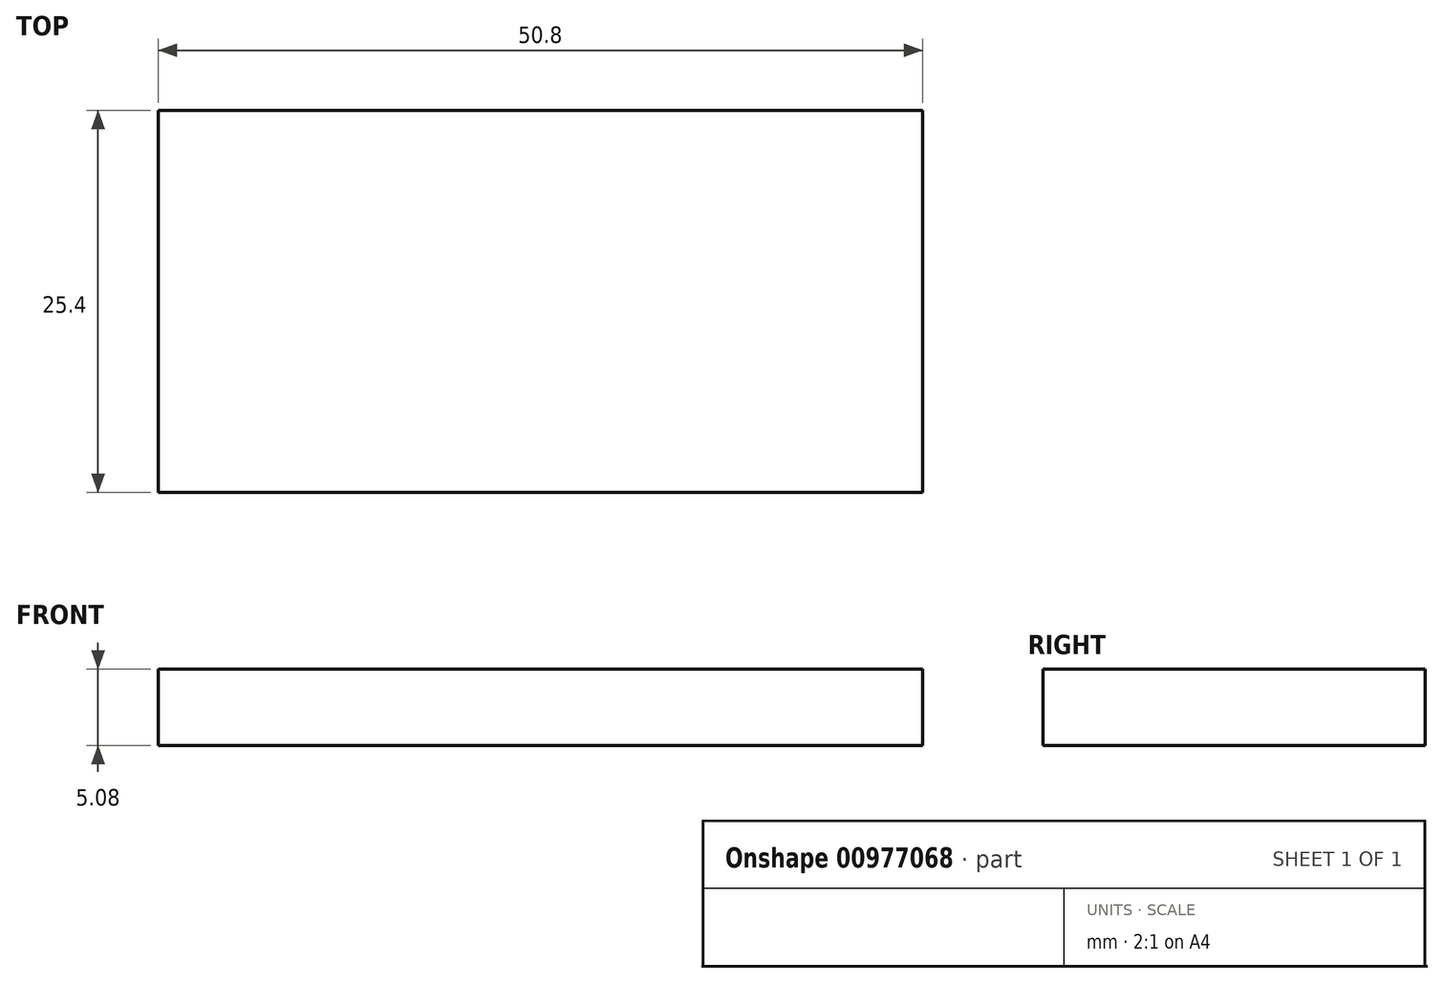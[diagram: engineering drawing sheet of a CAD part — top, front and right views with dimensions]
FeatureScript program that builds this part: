
annotation { "Feature Type Name" : "Feature", "Feature Type Description" : "" }
export const myFeature = defineFeature(function(context is Context, id is Id, definition is map)
    precondition{}
    {
        {
            var Q0;
            Q0=qCreatedBy(makeId("Top.planeOp"),FACE);
            var sketch = newSketch(context, id + "F0", { "sketchPlane" : qUnion([Q0])});
            skLineSegment(sketch, "E0.bottom", {"start": v(-25.4, 12.7) * mm, "end": v(25.4, 12.7) * mm});
            skLineSegment(sketch, "E0.top", {"start": v(-25.4, -12.7) * mm, "end": v(25.4, -12.7) * mm});
            skLineSegment(sketch, "E0.left", {"start": v(-25.4, 12.7) * mm, "end": v(-25.4, -12.7) * mm});
            skLineSegment(sketch, "E0.right", {"start": v(25.4, 12.7) * mm, "end": v(25.4, -12.7) * mm});
            skPoint(sketch, "E0.middle", {"position": v(0, 0) * mm});
            skSolve(sketch);
        }
        {
            var Q0;
            Q0=makeQuery(id+"F0.imprint","IMPRINT",FACE,{"disambiguationData":[TD([[makeQuery(id+"F0.imprint","IMPRINT",EDGE,{"derivedFrom":sQuery(id+"F0.wireOp",EDGE,"E0.bottom")}),-1.0]])]});
            extrude(context, id + "F1", {"entities" : qUnion([Q0]), "depth" : 5.08 * mm, "offsetDistance" : 25.4 * mm});
        }
    });
